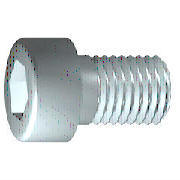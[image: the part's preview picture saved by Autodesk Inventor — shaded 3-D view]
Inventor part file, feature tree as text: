
AUTODESK INVENTOR PART (.ipt)
format: ipt  version: 2022 (Build 260153000, 153)  size: 192,512 bytes
history: native  units: mm (DEFAULTED — no unit token found)
features: sketch x2, other x1, extrude x1, plane x1, fillet x1
ambient origin geometry x7: Origin, YZ Plane, XY Plane, X Axis, Y Axis, Z Axis, Center Point
bodies: Solid1 (feature_tree)
feature tree (6):
  other  "Базовый элемент"
  extrude  "Паз"  Depth=10.875mm
  plane  "Work Plane1"
  fillet  "Fillet2"  Radius=0.276153mm
  sketch  "Эскиз1"
  sketch  "Эскиз2"
